# Revit family: Panel de gestión de cables
name_source: partatom
category: Equipement spécialisé
units: mm (PartAtom-declared; Revit-internal decimal feet)

## family parameters
Basée sur le plan de construction = Non
Cote de connecteur circulaire = Utiliser le diamètre
Couper avec des vides une fois chargée = Non
Partagée = Oui
Point de calcul de pièce = Non
Toujours verticalement = Oui
Type d'élément = Normal

## types (1)
- Accesorios de armarios
    Anchura (mm) = 482 mm  [stored 1.58136 ft]
    Clase de aplicación = EC000322
    Color = IDS_NOIR
    E-catalogo enlace = https://www.legrand.fr
    EAN = 3245060465223
    Elévation par défaut = 0 mm  [stored 0 ft]
    Formulación BIM = Accesorios de armarios
    Función = Gestión de cableado
    Longitud = 385
    Materia = Metal
    Modelo = Panel de interconexión
    Módulos de altura = 1
    Numero RAL = 9005
    Número de pieza Legrand = 046522
    Profundidad (mm) = 90 mm  [stored 0.295276 ft]

note: [stored X ft] marks values corroborated as IEEE doubles in the binary element streams (Revit-internal decimal feet)
